# Revit family: 379989
name_source: partatom
category: Specialty Equipment
revit_build: Autodesk Revit 2018 (Build: 20170223_1515(x64)
units: mm (PartAtom-declared; Revit-internal decimal feet)

## family parameters
Cut with Voids When Loaded = No
Host = Face
OmniClass Number = 23.40.20.21.14
OmniClass Title = Hand and Hair Dryers
Part Type = Normal
Room Calculation Point = No
Round Connector Dimension = Use Diameter
Shared = No

## types (2) — shared parameters
Body = Metal - Excel Dryer - Stainless Stainless - #4 Satin - Finish
Depth = 0' - 1"
Description = XChanger Kit
Keynote = 10 28 13
Manufacturer = Excel Dryer
Manufacturer Fax Number = 1-413-525-2853
Product Documentation Link = http://www.exceldryer.com
Product Name = XLERATOR XChanger Kit
Product Page URL = http://www.exceldryer.com
URL = http://www.exceldryer.com
Version = 2017 - v1.0b
Width = 1' - 5 1/4"

## per-type parameters (varying)
| type | Assembly Code | Default Elevation | Height | Model | Void Opening Height | XChanger Kit | XChanger Kit ADA |
| XLERATOR XChanger Kit | C1090.4040 | 2' - 7 1/16" | 4' - 8 1/8" | # 40575 XLERATOR XChanger Kit | 2' - 6" | Yes | No |
| XLERATOR XChanger Kit ADA | C1030200 | 4' - 0" | 4' - 8" | #40576 XLERATOR XChanger Kit ADA | 1' - 11" | No | Yes |

## geometry (parser evidence)
native form markers: Sweep x2
no freeform markers — native parametric forms only
